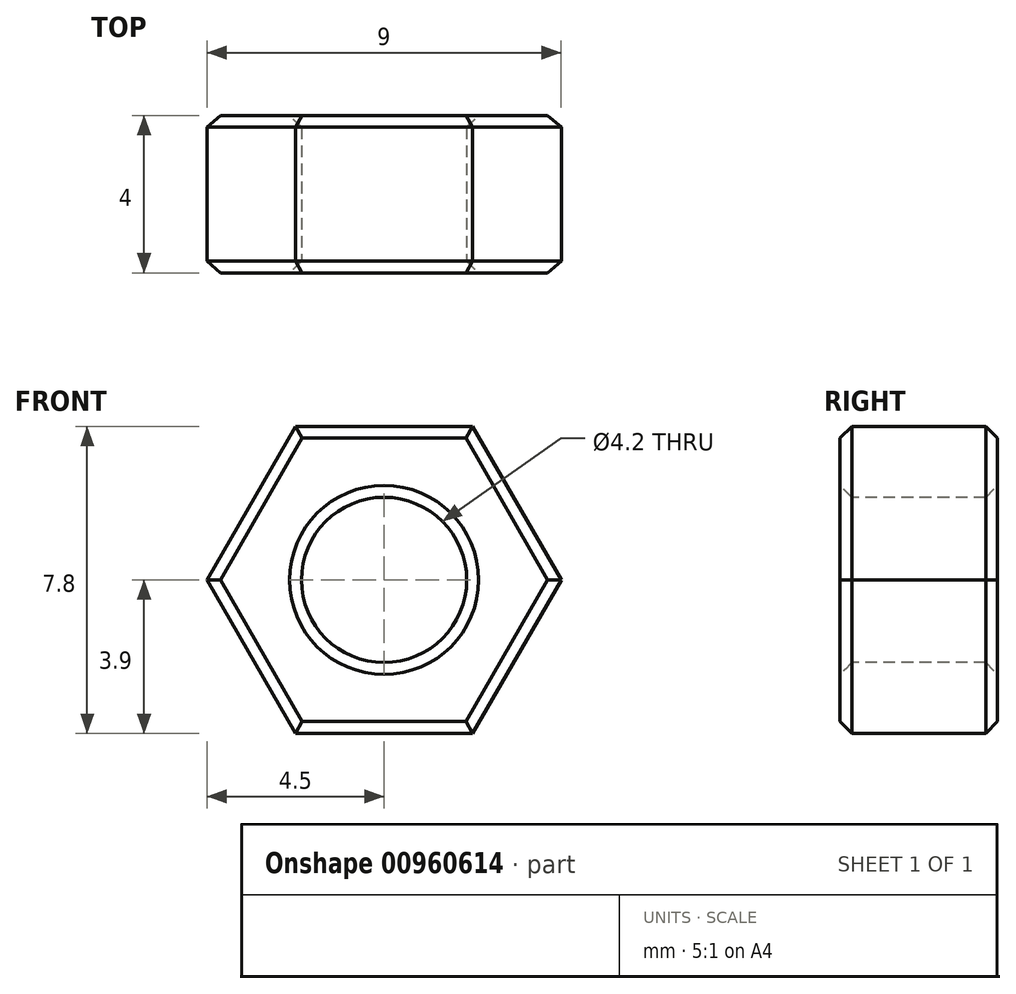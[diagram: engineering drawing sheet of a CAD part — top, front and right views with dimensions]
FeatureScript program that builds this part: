
annotation { "Feature Type Name" : "Feature", "Feature Type Description" : "" }
export const myFeature = defineFeature(function(context is Context, id is Id, definition is map)
    precondition{}
    {
        {
            var Q0;
            Q0=qCreatedBy(makeId("Front.planeOp"),FACE);
            var sketch = newSketch(context, id + "F0", { "sketchPlane" : qUnion([Q0])});
            skCircle(sketch, "E0.cCircle", {"center": v(0, 0) * mm, "radius": 3.9 * mm, "construction": true});
            skLineSegment(sketch, "E0.0", {"start": v(-2.25, 3.9) * mm, "end": v(2.25, 3.9) * mm});
            skLineSegment(sketch, "E0.1", {"start": v(2.25, 3.9) * mm, "end": v(4.5, 0) * mm});
            skLineSegment(sketch, "E0.2", {"start": v(4.5, 0) * mm, "end": v(2.25, -3.9) * mm});
            skLineSegment(sketch, "E0.3", {"start": v(2.25, -3.9) * mm, "end": v(-2.25, -3.9) * mm});
            skLineSegment(sketch, "E0.4", {"start": v(-2.25, -3.9) * mm, "end": v(-4.5, 0) * mm});
            skLineSegment(sketch, "E0.5", {"start": v(-4.5, 0) * mm, "end": v(-2.25, 3.9) * mm});
            skPoint(sketch, "E0.0.midPoint", {"position": v(0, 3.9) * mm});
            skSolve(sketch);
        }
        {
            var Q0;
            Q0=makeQuery(id+"F0.imprint","IMPRINT",FACE,{"disambiguationData":[TD([[makeQuery(id+"F0.imprint","IMPRINT",EDGE,{"derivedFrom":sQuery(id+"F0.wireOp",EDGE,"E0.0")}),-1.0]])]});
            extrude(context, id + "F1", {"entities" : qUnion([Q0]), "depth" : 4 * mm, "offsetDistance" : 25 * mm});
        }
        {
            var Q0;
            Q0=makeQuery(id+"F1.opExtrude","CAP_FACE",FACE,{"disambiguationData":[OSD([sQuery(id+"F0.wireOp",EDGE,"E0.0"),sQuery(id+"F0.wireOp",EDGE,"E0.1"),sQuery(id+"F0.wireOp",EDGE,"E0.2"),sQuery(id+"F0.wireOp",EDGE,"E0.3"),sQuery(id+"F0.wireOp",EDGE,"E0.4"),sQuery(id+"F0.wireOp",EDGE,"E0.5")])],"isStart":true});
            var sketch = newSketch(context, id + "F2", { "sketchPlane" : qUnion([Q0])});
            skPoint(sketch, "E1", {"position": v(0, 0) * mm});
            skSolve(sketch);
        }
        {
            var Q0;
            Q0=sQuery(id+"F2.wireOp",VERTEX,"E1");
            var Q1;
            Q1=makeQuery(id+"F1.opExtrude","SWEPT_BODY",BODY,{"disambiguationData":[OSD([sQuery(id+"F0.wireOp",EDGE,"E0.0"),sQuery(id+"F0.wireOp",EDGE,"E0.1"),sQuery(id+"F0.wireOp",EDGE,"E0.2"),sQuery(id+"F0.wireOp",EDGE,"E0.3"),sQuery(id+"F0.wireOp",EDGE,"E0.4"),sQuery(id+"F0.wireOp",EDGE,"E0.5")])]});
            hole(context, id + "F3", {"style" : HoleStyle.SIMPLE, "endStyle" : HoleEndStyle.THROUGH, "standardTappedOrClearance" : lookupTablePath({ "fit" : "Normal", "standard" : "ISO", "engagement" : "75%", "pitch" : "0.8 mm", "size" : "M5", "type" : "Tapped" }), "standardBlindInLast" : lookupTablePath({ "fit" : "Normal", "standard" : "ISO", "engagement" : "75%", "pitch" : "0.8 mm", "size" : "M5", "type" : "Clearance & tapped" }), "holeDiameter" : 4.2 * mm, "majorDiameter" : 5 * mm, "showTappedDepth" : true, "isTappedThrough" : true, "tappedDepth" : 12 * mm, "tapClearance" : 3, "locations" : qUnion([Q0]), "scope" : qUnion([Q1])});
        }
        {
            var Q0;
            Q0=makeQuery(id+"F1.opExtrude","CAP_EDGE",EDGE,{"disambiguationData":[OSD([sQuery(id+"F0.wireOp",EDGE,"E0.3")])],"isStart":true});
            var Q1;
            Q1=makeQuery(id+"F1.opExtrude","CAP_EDGE",EDGE,{"disambiguationData":[OSD([sQuery(id+"F0.wireOp",EDGE,"E0.4")])],"isStart":true});
            var Q2;
            Q2=makeQuery(id+"F1.opExtrude","CAP_EDGE",EDGE,{"disambiguationData":[OSD([sQuery(id+"F0.wireOp",EDGE,"E0.0")])],"isStart":true});
            var Q3;
            Q3=makeQuery(id+"F1.opExtrude","CAP_EDGE",EDGE,{"disambiguationData":[OSD([sQuery(id+"F0.wireOp",EDGE,"E0.5")])],"isStart":true});
            var Q4;
            Q4=makeQuery(id+"F1.opExtrude","CAP_FACE",FACE,{"disambiguationData":[OSD([sQuery(id+"F0.wireOp",EDGE,"E0.0"),sQuery(id+"F0.wireOp",EDGE,"E0.1"),sQuery(id+"F0.wireOp",EDGE,"E0.2"),sQuery(id+"F0.wireOp",EDGE,"E0.3"),sQuery(id+"F0.wireOp",EDGE,"E0.4"),sQuery(id+"F0.wireOp",EDGE,"E0.5")])],"isStart":true});
            var Q5;
            Q5=makeQuery(id+"F1.opExtrude","CAP_FACE",FACE,{"disambiguationData":[OSD([sQuery(id+"F0.wireOp",EDGE,"E0.0"),sQuery(id+"F0.wireOp",EDGE,"E0.1"),sQuery(id+"F0.wireOp",EDGE,"E0.2"),sQuery(id+"F0.wireOp",EDGE,"E0.3"),sQuery(id+"F0.wireOp",EDGE,"E0.4"),sQuery(id+"F0.wireOp",EDGE,"E0.5")])],"isStart":false});
            chamfer(context, id + "F4", {"entities" : qUnion([Q0, Q1, Q2, Q3, Q4, Q5]), "width" : 0.3 * mm, "tangentPropagation" : true});
        }
    });
